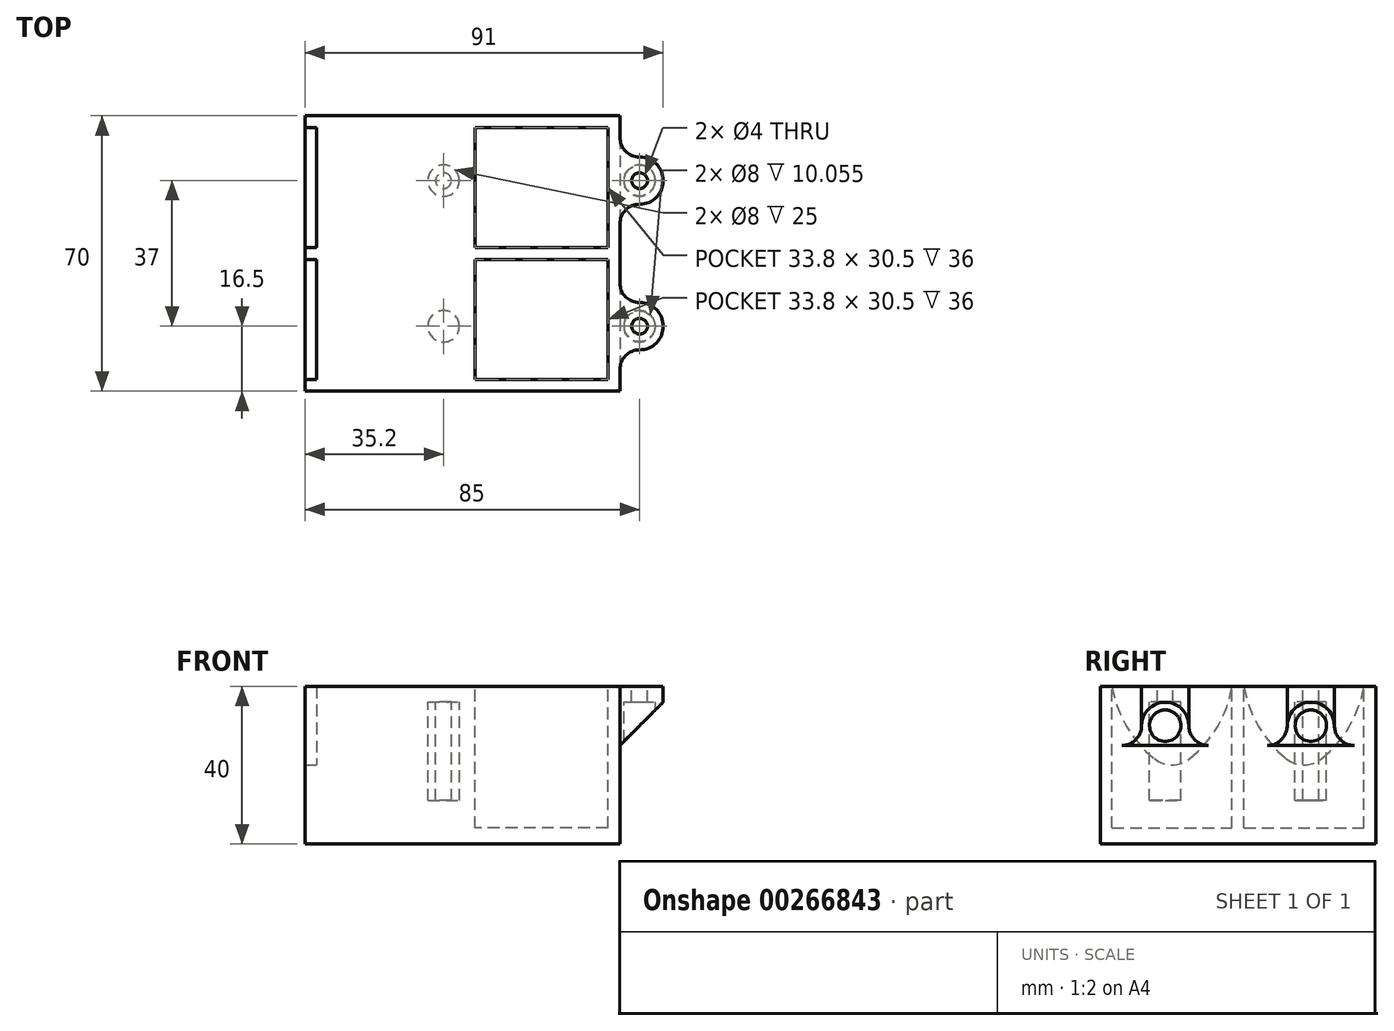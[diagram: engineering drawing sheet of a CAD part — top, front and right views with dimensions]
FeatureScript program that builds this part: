
annotation { "Feature Type Name" : "Feature", "Feature Type Description" : "" }
export const myFeature = defineFeature(function(context is Context, id is Id, definition is map)
    precondition{}
    {
        {
            var Q0;
            Q0=qCreatedBy(makeId("Top.planeOp"),FACE);
            var sketch = newSketch(context, id + "F0", { "sketchPlane" : qUnion([Q0])});
            skCircle(sketch, "E0", {"center": v(-24.9, 18.5) * mm, "radius": 2 * mm});
            skCircle(sketch, "E1", {"center": v(-24.9, -18.5) * mm, "radius": 2 * mm});
            skCircle(sketch, "E2", {"center": v(24.9, -18.5) * mm, "radius": 2 * mm});
            skCircle(sketch, "E3", {"center": v(24.9, 18.5) * mm, "radius": 2 * mm});
            skSolve(sketch);
        }
        {
            var Q0;
            Q0=qCreatedBy(makeId("Top.planeOp"),FACE);
            var sketch = newSketch(context, id + "F1", { "sketchPlane" : qUnion([Q0])});
            skCircle(sketch, "E4", {"center": v(24.9, 18.5) * mm, "radius": 6 * mm});
            skCircle(sketch, "E5", {"center": v(24.9, -18.5) * mm, "radius": 6 * mm});
            skCircle(sketch, "E6", {"center": v(-24.9, 18.5) * mm, "radius": 6 * mm});
            skCircle(sketch, "E7", {"center": v(-24.9, -18.5) * mm, "radius": 6 * mm});
            skSolve(sketch);
        }
        {
            var Q0;
            Q0=qCreatedBy(makeId("Top.planeOp"),FACE);
            var sketch = newSketch(context, id + "F2", { "sketchPlane" : qUnion([Q0])});
            skLineSegment(sketch, "E8.bottom", {"start": v(-60.1, 35) * mm, "end": v(19.9, 35) * mm});
            skLineSegment(sketch, "E8.top", {"start": v(-60.1, -35) * mm, "end": v(19.9, -35) * mm});
            skLineSegment(sketch, "E8.left", {"start": v(-60.1, 35) * mm, "end": v(-60.1, -35) * mm});
            skLineSegment(sketch, "E8.right", {"start": v(19.9, 35) * mm, "end": v(19.9, -35) * mm});
            skSolve(sketch);
        }
        {
            var Q0;
            Q0=makeQuery(id+"F1.imprint","IMPRINT",FACE,{"disambiguationData":[TD([[makeQuery(id+"F1.imprint","IMPRINT",EDGE,{"derivedFrom":sQuery(id+"F1.wireOp",EDGE,"E4")}),1.0]])]});
            var Q1;
            Q1=makeQuery(id+"F1.imprint","IMPRINT",FACE,{"disambiguationData":[TD([[makeQuery(id+"F1.imprint","IMPRINT",EDGE,{"derivedFrom":sQuery(id+"F1.wireOp",EDGE,"E5")}),1.0]])]});
            var Q2;
            Q2=makeQuery(id+"F1.imprint","IMPRINT",FACE,{"disambiguationData":[TD([[makeQuery(id+"F1.imprint","IMPRINT",EDGE,{"derivedFrom":sQuery(id+"F1.wireOp",EDGE,"E7")}),1.0]])]});
            var Q3;
            Q3=makeQuery(id+"F1.imprint","IMPRINT",FACE,{"disambiguationData":[TD([[makeQuery(id+"F1.imprint","IMPRINT",EDGE,{"derivedFrom":sQuery(id+"F1.wireOp",EDGE,"E6")}),1.0]])]});
            extrude(context, id + "F3", {"entities" : qUnion([Q0, Q1, Q2, Q3]), "oppositeDirection" : true, "depth" : 4 * mm});
        }
        {
            var Q0;
            Q0=makeQuery(id+"F0.imprint","IMPRINT",FACE,{"disambiguationData":[TD([[makeQuery(id+"F0.imprint","IMPRINT",EDGE,{"derivedFrom":sQuery(id+"F0.wireOp",EDGE,"E0")}),1.0]])]});
            var Q1;
            Q1=makeQuery(id+"F0.imprint","IMPRINT",FACE,{"disambiguationData":[TD([[makeQuery(id+"F0.imprint","IMPRINT",EDGE,{"derivedFrom":sQuery(id+"F0.wireOp",EDGE,"E1")}),1.0]])]});
            var Q2;
            Q2=makeQuery(id+"F0.imprint","IMPRINT",FACE,{"disambiguationData":[TD([[makeQuery(id+"F0.imprint","IMPRINT",EDGE,{"derivedFrom":sQuery(id+"F0.wireOp",EDGE,"E2")}),1.0]])]});
            var Q3;
            Q3=makeQuery(id+"F0.imprint","IMPRINT",FACE,{"disambiguationData":[TD([[makeQuery(id+"F0.imprint","IMPRINT",EDGE,{"derivedFrom":sQuery(id+"F0.wireOp",EDGE,"E3")}),1.0]])]});
            extrude(context, id + "F4", {"entities" : qUnion([Q0, Q1, Q2, Q3]), "oppositeDirection" : true, "depth" : 25 * mm});
        }
        {
            var Q0;
            Q0=makeQuery(id+"F4.opExtrude","SWEPT_BODY",BODY,{"disambiguationData":[OSD([sQuery(id+"F0.wireOp",EDGE,"E0")])]});
            var Q1;
            Q1=makeQuery(id+"F4.opExtrude","SWEPT_BODY",BODY,{"disambiguationData":[OSD([sQuery(id+"F0.wireOp",EDGE,"E1")])]});
            var Q2;
            Q2=makeQuery(id+"F4.opExtrude","SWEPT_BODY",BODY,{"disambiguationData":[OSD([sQuery(id+"F0.wireOp",EDGE,"E2")])]});
            var Q3;
            Q3=makeQuery(id+"F4.opExtrude","SWEPT_BODY",BODY,{"disambiguationData":[OSD([sQuery(id+"F0.wireOp",EDGE,"E3")])]});
            var Q4;
            Q4=makeQuery(id+"F3.opExtrude","SWEPT_BODY",BODY,{"disambiguationData":[OSD([sQuery(id+"F1.wireOp",EDGE,"E6")])]});
            var Q5;
            Q5=makeQuery(id+"F3.opExtrude","SWEPT_BODY",BODY,{"disambiguationData":[OSD([sQuery(id+"F1.wireOp",EDGE,"E7")])]});
            var Q6;
            Q6=makeQuery(id+"F3.opExtrude","SWEPT_BODY",BODY,{"disambiguationData":[OSD([sQuery(id+"F1.wireOp",EDGE,"E5")])]});
            var Q7;
            Q7=makeQuery(id+"F3.opExtrude","SWEPT_BODY",BODY,{"disambiguationData":[OSD([sQuery(id+"F1.wireOp",EDGE,"E4")])]});
            booleanBodies(context, id + "F5", {"operationType" : BooleanOperationType.SUBTRACTION, "tools" : qUnion([Q0, Q1, Q2, Q3]), "targets" : qUnion([Q4, Q5, Q6, Q7])});
        }
        {
            var Q0;
            Q0=makeQuery(id+"F2.imprint","IMPRINT",FACE,{"disambiguationData":[TD([[makeQuery(id+"F2.imprint","IMPRINT",EDGE,{"derivedFrom":sQuery(id+"F2.wireOp",EDGE,"E8.bottom")}),-1.0]])]});
            extrude(context, id + "F6", {"entities" : qUnion([Q0]), "oppositeDirection" : true, "depth" : 40 * mm});
        }
        {
            var Q0;
            Q0=makeQuery(id+"F6.opExtrude","CAP_FACE",FACE,{"disambiguationData":[OSD([sQuery(id+"F2.wireOp",EDGE,"E8.bottom"),sQuery(id+"F2.wireOp",EDGE,"E8.top"),sQuery(id+"F2.wireOp",EDGE,"E8.left"),sQuery(id+"F2.wireOp",EDGE,"E8.right")])],"isStart":true});
            var sketch = newSketch(context, id + "F7", { "sketchPlane" : qUnion([Q0])});
            skLineSegment(sketch, "E9.bottom", {"start": v(19.9, 35) * mm, "end": v(-60.1, 35) * mm});
            skLineSegment(sketch, "E9.top", {"start": v(19.9, 32) * mm, "end": v(-60.1, 32) * mm});
            skLineSegment(sketch, "E9.left", {"start": v(19.9, 35) * mm, "end": v(19.9, 32) * mm});
            skLineSegment(sketch, "E9.right", {"start": v(-60.1, 35) * mm, "end": v(-60.1, 32) * mm});
            skLineSegment(sketch, "E10.bottom", {"start": v(19.9, -35) * mm, "end": v(-60.1, -35) * mm});
            skLineSegment(sketch, "E10.top", {"start": v(19.9, -32) * mm, "end": v(-60.1, -32) * mm});
            skLineSegment(sketch, "E10.left", {"start": v(19.9, -35) * mm, "end": v(19.9, -32) * mm});
            skLineSegment(sketch, "E10.right", {"start": v(-60.1, -35) * mm, "end": v(-60.1, -32) * mm});
            skLineSegment(sketch, "E11.bottom", {"start": v(-60.1, 32) * mm, "end": v(-57.1, 32) * mm});
            skLineSegment(sketch, "E11.top", {"start": v(-60.1, -32) * mm, "end": v(-57.1, -32) * mm});
            skLineSegment(sketch, "E11.left", {"start": v(-60.1, 32) * mm, "end": v(-60.1, -32) * mm});
            skLineSegment(sketch, "E11.right", {"start": v(-57.1, 32) * mm, "end": v(-57.1, -32) * mm});
            skLineSegment(sketch, "E12.bottom", {"start": v(19.9, -32) * mm, "end": v(16.9, -32) * mm});
            skLineSegment(sketch, "E12.top", {"start": v(19.9, 32) * mm, "end": v(16.9, 32) * mm});
            skLineSegment(sketch, "E12.left", {"start": v(19.9, -32) * mm, "end": v(19.9, 32) * mm});
            skLineSegment(sketch, "E12.right", {"start": v(16.9, -32) * mm, "end": v(16.9, 32) * mm});
            skLineSegment(sketch, "E13.bottom", {"start": v(16.9, 1.5) * mm, "end": v(-57.1, 1.5) * mm});
            skLineSegment(sketch, "E13.top", {"start": v(16.9, -1.5) * mm, "end": v(-57.1, -1.5) * mm});
            skLineSegment(sketch, "E13.left", {"start": v(16.9, 1.5) * mm, "end": v(16.9, -1.5) * mm});
            skLineSegment(sketch, "E13.right", {"start": v(-57.1, 1.5) * mm, "end": v(-57.1, -1.5) * mm});
            skLineSegment(sketch, "E14.bottom", {"start": v(-17.1, 32) * mm, "end": v(-20.1, 32) * mm});
            skLineSegment(sketch, "E14.top", {"start": v(-17.1, 1.5) * mm, "end": v(-20.1, 1.5) * mm});
            skLineSegment(sketch, "E15.bottom", {"start": v(-17.1, -1.5) * mm, "end": v(-20.1, -1.5) * mm});
            skLineSegment(sketch, "E15.top", {"start": v(-17.1, -32) * mm, "end": v(-20.1, -32) * mm});
            skLineSegment(sketch, "E16.bottom", {"start": v(-16.9, -32) * mm, "end": v(-19.9, -32) * mm});
            skLineSegment(sketch, "E16.top", {"start": v(-16.9, 32) * mm, "end": v(-19.9, 32) * mm});
            skLineSegment(sketch, "E16.left", {"start": v(-16.9, -32) * mm, "end": v(-16.9, 32) * mm});
            skLineSegment(sketch, "E16.right", {"start": v(-19.9, -32) * mm, "end": v(-19.9, 32) * mm});
            skSolve(sketch);
        }
        {
            var Q0;
            Q0=makeQuery(id+"F6.opExtrude","CAP_FACE",FACE,{"disambiguationData":[OSD([sQuery(id+"F2.wireOp",EDGE,"E8.bottom"),sQuery(id+"F2.wireOp",EDGE,"E8.top"),sQuery(id+"F2.wireOp",EDGE,"E8.left"),sQuery(id+"F2.wireOp",EDGE,"E8.right")])],"isStart":true});
            var sketch = newSketch(context, id + "F8", { "sketchPlane" : qUnion([Q0])});
            skLineSegment(sketch, "E17.bottom", {"start": v(-57.1, 32) * mm, "end": v(-60.1, 32) * mm});
            skLineSegment(sketch, "E17.top", {"start": v(-57.1, 1.5) * mm, "end": v(-60.1, 1.5) * mm});
            skLineSegment(sketch, "E17.left", {"start": v(-57.1, 32) * mm, "end": v(-57.1, 1.5) * mm});
            skLineSegment(sketch, "E17.right", {"start": v(-60.1, 32) * mm, "end": v(-60.1, 1.5) * mm});
            skLineSegment(sketch, "E18.bottom", {"start": v(-57.1, -1.5) * mm, "end": v(-60.1, -1.5) * mm});
            skLineSegment(sketch, "E18.top", {"start": v(-57.1, -32) * mm, "end": v(-60.1, -32) * mm});
            skLineSegment(sketch, "E18.left", {"start": v(-57.1, -1.5) * mm, "end": v(-57.1, -32) * mm});
            skLineSegment(sketch, "E18.right", {"start": v(-60.1, -1.5) * mm, "end": v(-60.1, -32) * mm});
            skSolve(sketch);
        }
        {
            var Q0;
            Q0=makeQuery(id+"F8.imprint","IMPRINT",FACE,{"disambiguationData":[TD([[makeQuery(id+"F8.imprint","IMPRINT",EDGE,{"derivedFrom":sQuery(id+"F8.wireOp",EDGE,"E17.bottom")}),1.0]])]});
            var Q1;
            Q1=makeQuery(id+"F8.imprint","IMPRINT",FACE,{"disambiguationData":[TD([[makeQuery(id+"F8.imprint","IMPRINT",EDGE,{"derivedFrom":sQuery(id+"F8.wireOp",EDGE,"E18.bottom")}),1.0]])]});
            extrude(context, id + "F9", {"entities" : qUnion([Q0, Q1]), "oppositeDirection" : true, "depth" : 25 * mm});
        }
        {
            var Q0;
            Q0=makeQuery(id+"F9.opExtrude","SWEPT_BODY",BODY,{"disambiguationData":[OSD([sQuery(id+"F8.wireOp",EDGE,"E17.bottom"),sQuery(id+"F8.wireOp",EDGE,"E17.top"),sQuery(id+"F8.wireOp",EDGE,"E17.left"),sQuery(id+"F8.wireOp",EDGE,"E17.right")])]});
            var Q1;
            Q1=makeQuery(id+"F9.opExtrude","SWEPT_BODY",BODY,{"disambiguationData":[OSD([sQuery(id+"F8.wireOp",EDGE,"E18.bottom"),sQuery(id+"F8.wireOp",EDGE,"E18.top"),sQuery(id+"F8.wireOp",EDGE,"E18.left"),sQuery(id+"F8.wireOp",EDGE,"E18.right")])]});
            var Q2;
            Q2=makeQuery(id+"F6.opExtrude","SWEPT_BODY",BODY,{"disambiguationData":[OSD([sQuery(id+"F2.wireOp",EDGE,"E8.bottom"),sQuery(id+"F2.wireOp",EDGE,"E8.top"),sQuery(id+"F2.wireOp",EDGE,"E8.left"),sQuery(id+"F2.wireOp",EDGE,"E8.right")])]});
            booleanBodies(context, id + "F10", {"operationType" : BooleanOperationType.SUBTRACTION, "tools" : qUnion([Q0, Q1]), "targets" : qUnion([Q2])});
        }
        {
            var Q0;
            Q0=makeQuery(id+"F3.opExtrude","CAP_FACE",FACE,{"disambiguationData":[OSD([sQuery(id+"F1.wireOp",EDGE,"E6")])],"isStart":false});
            var sketch = newSketch(context, id + "F11", { "sketchPlane" : qUnion([Q0])});
            skCircle(sketch, "E19", {"center": v(-24.9, -18.5) * mm, "radius": 4 * mm});
            skCircle(sketch, "E20", {"center": v(-24.9, 18.5) * mm, "radius": 4 * mm});
            skCircle(sketch, "E21", {"center": v(24.9, 18.5) * mm, "radius": 4 * mm});
            skCircle(sketch, "E22", {"center": v(24.9, -18.5) * mm, "radius": 4 * mm});
            skSolve(sketch);
        }
        {
            var Q0;
            {var subQ9=sQuery(id+"F7.wireOp",EDGE,"E15.top");Q0=makeQuery(id+"F7.imprint","IMPRINT",FACE,{"disambiguationData":[TD([[makeQuery(id+"F7.imprint","IMPRINT",EDGE,{"derivedFrom":subQ9}),-1.0]])]});}
            var Q1;
            {var subQ3=sQuery(id+"F7.wireOp",EDGE,"E16.left");var subQ5=sQuery(id+"F7.wireOp",EDGE,"E13.top");var subQ7=makeQuery(id+"F7.imprint","INTERSECT",VERTEX,{"derivedFrom":[subQ5,subQ3]});Q1=makeQuery(id+"F7.imprint","IMPRINT",FACE,{"disambiguationData":[TD([[makeQuery(id+"F7.imprint","IMPRINT",EDGE,{"disambiguationData":[TD([[subQ7,1.0]])],"derivedFrom":subQ5}),1.0]])]});}
            var Q2;
            {var subQ0=sQuery(id+"F7.wireOp",EDGE,"E14.bottom");Q2=makeQuery(id+"F7.imprint","IMPRINT",FACE,{"disambiguationData":[TD([[makeQuery(id+"F7.imprint","IMPRINT",EDGE,{"derivedFrom":subQ0}),1.0]])]});}
            var Q3;
            {var subQ3=sQuery(id+"F7.wireOp",EDGE,"E16.left");var subQ5=sQuery(id+"F7.wireOp",EDGE,"E13.bottom");var subQ7=makeQuery(id+"F7.imprint","INTERSECT",VERTEX,{"derivedFrom":[subQ5,subQ3]});Q3=makeQuery(id+"F7.imprint","IMPRINT",FACE,{"disambiguationData":[TD([[makeQuery(id+"F7.imprint","IMPRINT",EDGE,{"disambiguationData":[TD([[subQ7,1.0]])],"derivedFrom":subQ5}),-1.0]])]});}
            extrude(context, id + "F12", {"entities" : qUnion([Q0, Q1, Q2, Q3]), "oppositeDirection" : true, "depth" : 36 * mm});
        }
        {
            var Q0;
            Q0=makeQuery(id+"F12.opExtrude","SWEPT_BODY",BODY,{"disambiguationData":[OSD([sQuery(id+"F7.wireOp",EDGE,"E10.top"),sQuery(id+"F7.wireOp",EDGE,"E12.right"),sQuery(id+"F7.wireOp",EDGE,"E13.top"),sQuery(id+"F7.wireOp",EDGE,"E16.left")])]});
            var Q1;
            Q1=makeQuery(id+"F12.opExtrude","SWEPT_BODY",BODY,{"disambiguationData":[OSD([sQuery(id+"F7.wireOp",EDGE,"E10.top"),sQuery(id+"F7.wireOp",EDGE,"E11.right"),sQuery(id+"F7.wireOp",EDGE,"E13.top"),sQuery(id+"F7.wireOp",EDGE,"E15.bottom"),sQuery(id+"F7.wireOp",EDGE,"E15.top"),sQuery(id+"F7.wireOp",EDGE,"E16.right")])]});
            var Q2;
            Q2=makeQuery(id+"F12.opExtrude","SWEPT_BODY",BODY,{"disambiguationData":[OSD([sQuery(id+"F7.wireOp",EDGE,"E9.top"),sQuery(id+"F7.wireOp",EDGE,"E12.right"),sQuery(id+"F7.wireOp",EDGE,"E13.bottom"),sQuery(id+"F7.wireOp",EDGE,"E16.left")])]});
            var Q3;
            Q3=makeQuery(id+"F12.opExtrude","SWEPT_BODY",BODY,{"disambiguationData":[OSD([sQuery(id+"F7.wireOp",EDGE,"E9.top"),sQuery(id+"F7.wireOp",EDGE,"E11.right"),sQuery(id+"F7.wireOp",EDGE,"E13.bottom"),sQuery(id+"F7.wireOp",EDGE,"E14.bottom"),sQuery(id+"F7.wireOp",EDGE,"E14.top"),sQuery(id+"F7.wireOp",EDGE,"E16.right")])]});
            var Q4;
            Q4=makeQuery(id+"F6.opExtrude","SWEPT_BODY",BODY,{"disambiguationData":[OSD([sQuery(id+"F2.wireOp",EDGE,"E8.bottom"),sQuery(id+"F2.wireOp",EDGE,"E8.top"),sQuery(id+"F2.wireOp",EDGE,"E8.left"),sQuery(id+"F2.wireOp",EDGE,"E8.right")])]});
            booleanBodies(context, id + "F13", {"operationType" : BooleanOperationType.SUBTRACTION, "tools" : qUnion([Q0, Q1, Q2, Q3]), "targets" : qUnion([Q4])});
        }
        {
            var Q0;
            Q0=makeQuery(id+"F3.opExtrude","SWEPT_BODY",BODY,{"disambiguationData":[OSD([sQuery(id+"F1.wireOp",EDGE,"E6")])]});
            var Q1;
            Q1=makeQuery(id+"F3.opExtrude","SWEPT_BODY",BODY,{"disambiguationData":[OSD([sQuery(id+"F1.wireOp",EDGE,"E7")])]});
            var Q2;
            Q2=makeQuery(id+"F3.opExtrude","SWEPT_BODY",BODY,{"disambiguationData":[OSD([sQuery(id+"F1.wireOp",EDGE,"E4")])]});
            var Q3;
            Q3=makeQuery(id+"F3.opExtrude","SWEPT_BODY",BODY,{"disambiguationData":[OSD([sQuery(id+"F1.wireOp",EDGE,"E5")])]});
            var Q4;
            Q4=makeQuery(id+"F6.opExtrude","SWEPT_BODY",BODY,{"disambiguationData":[OSD([sQuery(id+"F2.wireOp",EDGE,"E8.bottom"),sQuery(id+"F2.wireOp",EDGE,"E8.top"),sQuery(id+"F2.wireOp",EDGE,"E8.left"),sQuery(id+"F2.wireOp",EDGE,"E8.right")])]});
            booleanBodies(context, id + "F14", {"operationType" : BooleanOperationType.UNION, "tools" : qUnion([Q0, Q1, Q2, Q3, Q4])});
        }
        {
            var Q0;
            {var subQ0=sQuery(id+"F7.wireOp",EDGE,"E16.right");Q0=makeQuery(id+"F14.opBoolean","INTERSECT",EDGE,{"derivedFrom":[makeQuery(id+"F3.opExtrude","CAP_FACE",FACE,{"disambiguationData":[OSD([sQuery(id+"F1.wireOp",EDGE,"E6")])],"isStart":false}),makeQuery(id+"F13.opBoolean","COPY",FACE,{"derivedFrom":makeQuery(id+"F12.opExtrude","SWEPT_FACE",FACE,{"disambiguationData":[OSD([subQ0]),TDD([makeQuery(id+"F7.imprint","IMPRINT",EDGE,{"disambiguationData":[TD([[makeQuery(id+"F7.imprint","INTERSECT",VERTEX,{"derivedFrom":[sQuery(id+"F7.wireOp",EDGE,"E14.top"),subQ0]}),-1.0]])],"derivedFrom":subQ0})])]})})]});}
            var Q1;
            {var subQ0=sQuery(id+"F7.wireOp",EDGE,"E16.right");Q1=makeQuery(id+"F14.opBoolean","INTERSECT",EDGE,{"derivedFrom":[makeQuery(id+"F3.opExtrude","CAP_FACE",FACE,{"disambiguationData":[OSD([sQuery(id+"F1.wireOp",EDGE,"E7")])],"isStart":false}),makeQuery(id+"F13.opBoolean","COPY",FACE,{"derivedFrom":makeQuery(id+"F12.opExtrude","SWEPT_FACE",FACE,{"disambiguationData":[OSD([subQ0]),TDD([makeQuery(id+"F7.imprint","IMPRINT",EDGE,{"disambiguationData":[TD([[makeQuery(id+"F7.imprint","INTERSECT",VERTEX,{"derivedFrom":[sQuery(id+"F7.wireOp",EDGE,"E15.bottom"),subQ0]}),1.0]])],"derivedFrom":subQ0})])]})})]});}
            var Q2;
            Q2=makeQuery(id+"F14.opBoolean","INTERSECT",EDGE,{"derivedFrom":[makeQuery(id+"F3.opExtrude","CAP_FACE",FACE,{"disambiguationData":[OSD([sQuery(id+"F1.wireOp",EDGE,"E5")])],"isStart":false}),makeQuery(id+"F6.opExtrude","SWEPT_FACE",FACE,{"disambiguationData":[OSD([sQuery(id+"F2.wireOp",EDGE,"E8.right")])]})]});
            var Q3;
            Q3=makeQuery(id+"F14.opBoolean","INTERSECT",EDGE,{"derivedFrom":[makeQuery(id+"F3.opExtrude","CAP_FACE",FACE,{"disambiguationData":[OSD([sQuery(id+"F1.wireOp",EDGE,"E4")])],"isStart":false}),makeQuery(id+"F6.opExtrude","SWEPT_FACE",FACE,{"disambiguationData":[OSD([sQuery(id+"F2.wireOp",EDGE,"E8.right")])]})]});
            chamfer(context, id + "F15", {"entities" : qUnion([Q0, Q1, Q2, Q3]), "width" : 11 * mm, "tangentPropagation" : true});
        }
        {
            var Q0;
            Q0=makeQuery(id+"F11.imprint","IMPRINT",FACE,{"disambiguationData":[TD([[makeQuery(id+"F11.imprint","IMPRINT",EDGE,{"derivedFrom":sQuery(id+"F11.wireOp",EDGE,"E22")}),1.0]])]});
            var Q1;
            Q1=makeQuery(id+"F11.imprint","IMPRINT",FACE,{"disambiguationData":[TD([[makeQuery(id+"F11.imprint","IMPRINT",EDGE,{"derivedFrom":sQuery(id+"F11.wireOp",EDGE,"E21")}),1.0]])]});
            var Q2;
            Q2=makeQuery(id+"F11.imprint","IMPRINT",FACE,{"disambiguationData":[TD([[makeQuery(id+"F11.imprint","IMPRINT",EDGE,{"derivedFrom":sQuery(id+"F11.wireOp",EDGE,"E19")}),1.0]])]});
            var Q3;
            Q3=makeQuery(id+"F11.imprint","IMPRINT",FACE,{"disambiguationData":[TD([[makeQuery(id+"F11.imprint","IMPRINT",EDGE,{"derivedFrom":sQuery(id+"F11.wireOp",EDGE,"E20")}),1.0]])]});
            extrude(context, id + "F16", {"entities" : qUnion([Q0, Q1, Q2, Q3]), "depth" : 25 * mm});
        }
        {
            var Q0;
            Q0=makeQuery(id+"F16.opExtrude","SWEPT_BODY",BODY,{"disambiguationData":[OSD([sQuery(id+"F0.wireOp",EDGE,"E0"),sQuery(id+"F1.wireOp",EDGE,"E6"),sQuery(id+"F11.wireOp",EDGE,"E19")])]});
            var Q1;
            Q1=makeQuery(id+"F16.opExtrude","SWEPT_BODY",BODY,{"disambiguationData":[OSD([sQuery(id+"F11.wireOp",EDGE,"E20")])]});
            var Q2;
            Q2=makeQuery(id+"F16.opExtrude","SWEPT_BODY",BODY,{"disambiguationData":[OSD([sQuery(id+"F11.wireOp",EDGE,"E21")])]});
            var Q3;
            Q3=makeQuery(id+"F16.opExtrude","SWEPT_BODY",BODY,{"disambiguationData":[OSD([sQuery(id+"F11.wireOp",EDGE,"E22")])]});
            var Q4;
            Q4=makeQuery(id+"F3.opExtrude","SWEPT_BODY",BODY,{"disambiguationData":[OSD([sQuery(id+"F1.wireOp",EDGE,"E6")])]});
            booleanBodies(context, id + "F17", {"operationType" : BooleanOperationType.SUBTRACTION, "tools" : qUnion([Q0, Q1, Q2, Q3]), "targets" : qUnion([Q4])});
        }
        {
            var Q0;
            Q0=makeQuery(id+"F10.opBoolean","COPY",EDGE,{"derivedFrom":makeQuery(id+"F9.opExtrude","CAP_EDGE",EDGE,{"disambiguationData":[OSD([sQuery(id+"F8.wireOp",EDGE,"E17.bottom")])],"isStart":false})});
            var Q1;
            Q1=makeQuery(id+"F10.opBoolean","COPY",EDGE,{"derivedFrom":makeQuery(id+"F9.opExtrude","CAP_EDGE",EDGE,{"disambiguationData":[OSD([sQuery(id+"F8.wireOp",EDGE,"E18.bottom")])],"isStart":false})});
            var Q2;
            Q2=makeQuery(id+"F10.opBoolean","COPY",EDGE,{"derivedFrom":makeQuery(id+"F9.opExtrude","CAP_EDGE",EDGE,{"disambiguationData":[OSD([sQuery(id+"F8.wireOp",EDGE,"E17.top")])],"isStart":false})});
            var Q3;
            Q3=makeQuery(id+"F10.opBoolean","COPY",EDGE,{"derivedFrom":makeQuery(id+"F9.opExtrude","CAP_EDGE",EDGE,{"disambiguationData":[OSD([sQuery(id+"F8.wireOp",EDGE,"E18.top")])],"isStart":false})});
            fillet(context, id + "F18", {"entities" : qUnion([Q0, Q1, Q2, Q3]), "radius" : 30 * mm, "tangentPropagation" : true, "allowEdgeOverflow" : false});
        }
        {
            var Q0;
            Q0=makeQuery(id+"F18.opFillet","BLEND_EDGE",EDGE,{"blendedFrom":[makeQuery(id+"F10.opBoolean","COPY",EDGE,{"derivedFrom":makeQuery(id+"F9.opExtrude","CAP_EDGE",EDGE,{"disambiguationData":[OSD([sQuery(id+"F8.wireOp",EDGE,"E17.bottom")])],"isStart":false})}),makeQuery(id+"F10.opBoolean","COPY",EDGE,{"derivedFrom":makeQuery(id+"F9.opExtrude","CAP_EDGE",EDGE,{"disambiguationData":[OSD([sQuery(id+"F8.wireOp",EDGE,"E17.top")])],"isStart":false})})],"blendedInto":[]});
            var Q1;
            Q1=makeQuery(id+"F18.opFillet","BLEND_EDGE",EDGE,{"blendedFrom":[makeQuery(id+"F10.opBoolean","COPY",EDGE,{"derivedFrom":makeQuery(id+"F9.opExtrude","CAP_EDGE",EDGE,{"disambiguationData":[OSD([sQuery(id+"F8.wireOp",EDGE,"E18.bottom")])],"isStart":false})}),makeQuery(id+"F10.opBoolean","COPY",EDGE,{"derivedFrom":makeQuery(id+"F9.opExtrude","CAP_EDGE",EDGE,{"disambiguationData":[OSD([sQuery(id+"F8.wireOp",EDGE,"E18.top")])],"isStart":false})})],"blendedInto":[]});
            fillet(context, id + "F19", {"entities" : qUnion([Q0, Q1]), "radius" : 7.23 * mm, "tangentPropagation" : true, "allowEdgeOverflow" : false});
        }
        {
            var Q0;
            Q0=makeQuery(id+"F14.opBoolean","INTERSECT",EDGE,{"disambiguationData":[OD(0.0)],"derivedFrom":[makeQuery(id+"F3.opExtrude","SWEPT_FACE",FACE,{"disambiguationData":[OSD([sQuery(id+"F1.wireOp",EDGE,"E5")])]}),makeQuery(id+"F6.opExtrude","SWEPT_FACE",FACE,{"disambiguationData":[OSD([sQuery(id+"F2.wireOp",EDGE,"E8.right")])]})]});
            var Q1;
            Q1=makeQuery(id+"F14.opBoolean","INTERSECT",EDGE,{"disambiguationData":[OD(1.0)],"derivedFrom":[makeQuery(id+"F3.opExtrude","SWEPT_FACE",FACE,{"disambiguationData":[OSD([sQuery(id+"F1.wireOp",EDGE,"E5")])]}),makeQuery(id+"F6.opExtrude","SWEPT_FACE",FACE,{"disambiguationData":[OSD([sQuery(id+"F2.wireOp",EDGE,"E8.right")])]})]});
            var Q2;
            Q2=makeQuery(id+"F14.opBoolean","INTERSECT",EDGE,{"disambiguationData":[OD(1.0)],"derivedFrom":[makeQuery(id+"F3.opExtrude","SWEPT_FACE",FACE,{"disambiguationData":[OSD([sQuery(id+"F1.wireOp",EDGE,"E4")])]}),makeQuery(id+"F6.opExtrude","SWEPT_FACE",FACE,{"disambiguationData":[OSD([sQuery(id+"F2.wireOp",EDGE,"E8.right")])]})]});
            fillet(context, id + "F20", {"entities" : qUnion([Q0, Q1, Q2]), "radius" : 5 * mm, "tangentPropagation" : true, "allowEdgeOverflow" : false});
        }
        {
            var Q0;
            Q0=makeQuery(id+"F14.opBoolean","INTERSECT",EDGE,{"disambiguationData":[OD(0.0)],"derivedFrom":[makeQuery(id+"F3.opExtrude","SWEPT_FACE",FACE,{"disambiguationData":[OSD([sQuery(id+"F1.wireOp",EDGE,"E4")])]}),makeQuery(id+"F6.opExtrude","SWEPT_FACE",FACE,{"disambiguationData":[OSD([sQuery(id+"F2.wireOp",EDGE,"E8.right")])]})]});
            var Q1;
            {var subQ0=sQuery(id+"F7.wireOp",EDGE,"E16.right");Q1=makeQuery(id+"F14.opBoolean","INTERSECT",EDGE,{"disambiguationData":[OD(1.0)],"derivedFrom":[makeQuery(id+"F3.opExtrude","SWEPT_FACE",FACE,{"disambiguationData":[OSD([sQuery(id+"F1.wireOp",EDGE,"E7")])]}),makeQuery(id+"F13.opBoolean","COPY",FACE,{"derivedFrom":makeQuery(id+"F12.opExtrude","SWEPT_FACE",FACE,{"disambiguationData":[OSD([subQ0]),TDD([makeQuery(id+"F7.imprint","IMPRINT",EDGE,{"disambiguationData":[TD([[makeQuery(id+"F7.imprint","INTERSECT",VERTEX,{"derivedFrom":[sQuery(id+"F7.wireOp",EDGE,"E15.bottom"),subQ0]}),1.0]])],"derivedFrom":subQ0})])]})})]});}
            var Q2;
            {var subQ0=sQuery(id+"F7.wireOp",EDGE,"E16.right");Q2=makeQuery(id+"F14.opBoolean","INTERSECT",EDGE,{"disambiguationData":[OD(0.0)],"derivedFrom":[makeQuery(id+"F3.opExtrude","SWEPT_FACE",FACE,{"disambiguationData":[OSD([sQuery(id+"F1.wireOp",EDGE,"E6")])]}),makeQuery(id+"F13.opBoolean","COPY",FACE,{"derivedFrom":makeQuery(id+"F12.opExtrude","SWEPT_FACE",FACE,{"disambiguationData":[OSD([subQ0]),TDD([makeQuery(id+"F7.imprint","IMPRINT",EDGE,{"disambiguationData":[TD([[makeQuery(id+"F7.imprint","INTERSECT",VERTEX,{"derivedFrom":[sQuery(id+"F7.wireOp",EDGE,"E14.top"),subQ0]}),-1.0]])],"derivedFrom":subQ0})])]})})]});}
            var Q3;
            {var subQ0=sQuery(id+"F7.wireOp",EDGE,"E16.right");Q3=makeQuery(id+"F14.opBoolean","INTERSECT",EDGE,{"disambiguationData":[OD(1.0)],"derivedFrom":[makeQuery(id+"F3.opExtrude","SWEPT_FACE",FACE,{"disambiguationData":[OSD([sQuery(id+"F1.wireOp",EDGE,"E6")])]}),makeQuery(id+"F13.opBoolean","COPY",FACE,{"derivedFrom":makeQuery(id+"F12.opExtrude","SWEPT_FACE",FACE,{"disambiguationData":[OSD([subQ0]),TDD([makeQuery(id+"F7.imprint","IMPRINT",EDGE,{"disambiguationData":[TD([[makeQuery(id+"F7.imprint","INTERSECT",VERTEX,{"derivedFrom":[sQuery(id+"F7.wireOp",EDGE,"E14.top"),subQ0]}),-1.0]])],"derivedFrom":subQ0})])]})})]});}
            var Q4;
            {var subQ0=sQuery(id+"F7.wireOp",EDGE,"E16.right");Q4=makeQuery(id+"F14.opBoolean","INTERSECT",EDGE,{"disambiguationData":[OD(0.0)],"derivedFrom":[makeQuery(id+"F3.opExtrude","SWEPT_FACE",FACE,{"disambiguationData":[OSD([sQuery(id+"F1.wireOp",EDGE,"E7")])]}),makeQuery(id+"F13.opBoolean","COPY",FACE,{"derivedFrom":makeQuery(id+"F12.opExtrude","SWEPT_FACE",FACE,{"disambiguationData":[OSD([subQ0]),TDD([makeQuery(id+"F7.imprint","IMPRINT",EDGE,{"disambiguationData":[TD([[makeQuery(id+"F7.imprint","INTERSECT",VERTEX,{"derivedFrom":[sQuery(id+"F7.wireOp",EDGE,"E15.bottom"),subQ0]}),1.0]])],"derivedFrom":subQ0})])]})})]});}
            fillet(context, id + "F21", {"entities" : qUnion([Q0, Q1, Q2, Q3, Q4]), "radius" : 5 * mm, "tangentPropagation" : true, "allowEdgeOverflow" : false});
        }
    });
